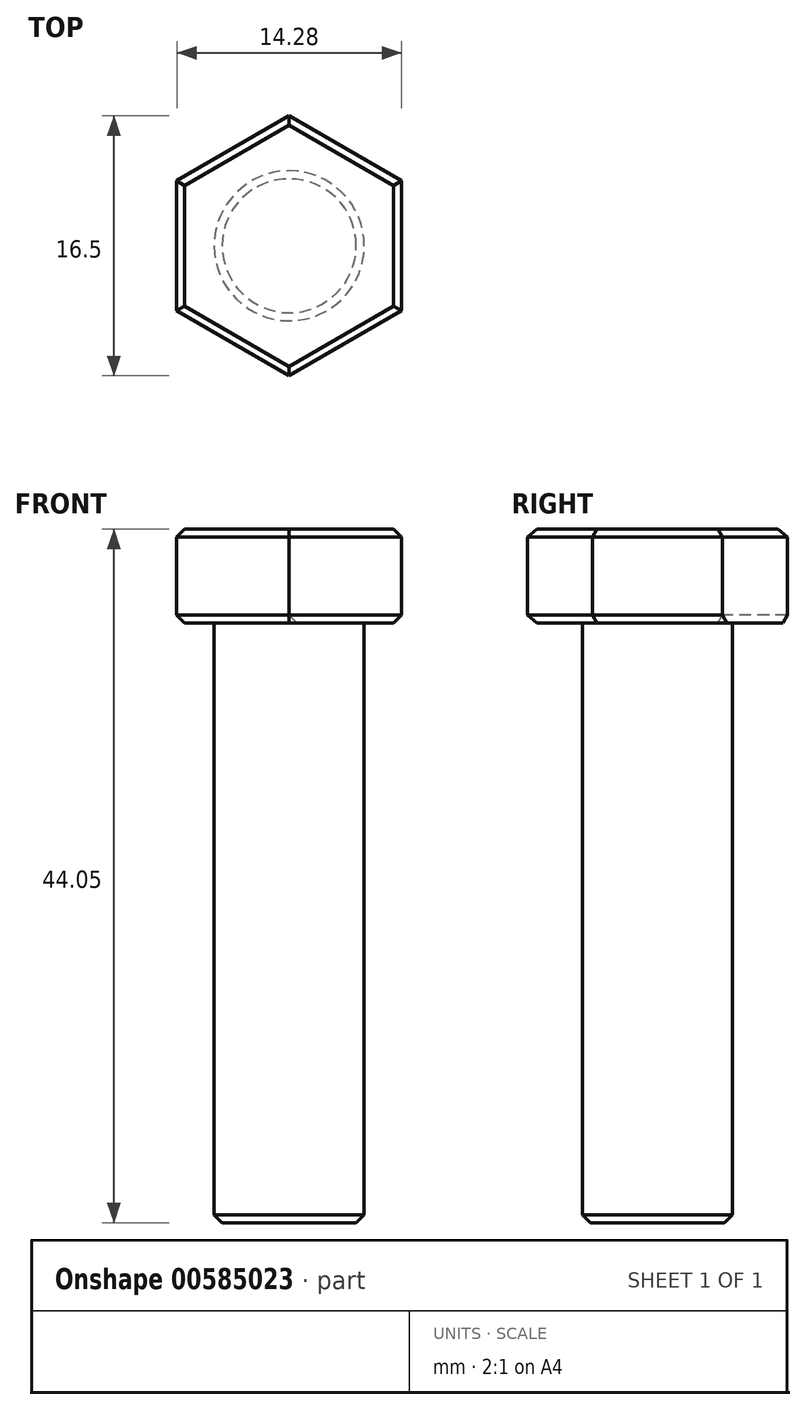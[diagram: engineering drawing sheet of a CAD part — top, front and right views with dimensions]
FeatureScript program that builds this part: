
annotation { "Feature Type Name" : "Feature", "Feature Type Description" : "" }
export const myFeature = defineFeature(function(context is Context, id is Id, definition is map)
    precondition{}
    {
        {
            var Q0;
            Q0=qCreatedBy(makeId("Top.planeOp"),FACE);
            var sketch = newSketch(context, id + "F0", { "sketchPlane" : qUnion([Q0])});
            skCircle(sketch, "E0.cCircle", {"center": v(0, 0) * mm, "radius": 7.14 * mm, "construction": true});
            skLineSegment(sketch, "E0.0", {"start": v(7.14, 4.12) * mm, "end": v(7.14, -4.12) * mm});
            skLineSegment(sketch, "E0.1", {"start": v(7.14, -4.12) * mm, "end": v(0, -8.25) * mm});
            skLineSegment(sketch, "E0.2", {"start": v(0, -8.25) * mm, "end": v(-7.14, -4.12) * mm});
            skLineSegment(sketch, "E0.3", {"start": v(-7.14, -4.12) * mm, "end": v(-7.14, 4.12) * mm});
            skLineSegment(sketch, "E0.4", {"start": v(-7.14, 4.12) * mm, "end": v(0, 8.25) * mm});
            skLineSegment(sketch, "E0.5", {"start": v(0, 8.25) * mm, "end": v(7.14, 4.12) * mm});
            skPoint(sketch, "E0.0.midPoint", {"position": v(7.14, 0) * mm});
            skCircle(sketch, "E1", {"center": v(0, 0) * mm, "radius": 4.76 * mm});
            skSolve(sketch);
        }
        {
            var Q0;
            Q0 = qSketchRegion(id + "F0", true);
            var Q1;
            Q1=makeQuery(id+"F0.imprint","IMPRINT",FACE,{"disambiguationData":[TD([[makeQuery(id+"F0.imprint","IMPRINT",EDGE,{"derivedFrom":sQuery(id+"F0.wireOp",EDGE,"E1")}),1.0]])]});
            extrude(context, id + "F1", {"entities" : qUnion([Q0, Q1]), "depth" : 5.95 * mm, "offsetDistance" : 25.4 * mm});
        }
        {
            var Q0;
            Q0=makeQuery(id+"F0.imprint","IMPRINT",FACE,{"disambiguationData":[TD([[makeQuery(id+"F0.imprint","IMPRINT",EDGE,{"derivedFrom":sQuery(id+"F0.wireOp",EDGE,"E1")}),1.0]])]});
            extrude(context, id + "F2", {"entities" : qUnion([Q0]), "operationType" : NewBodyOperationType.ADD, "oppositeDirection" : true, "depth" : 38.1 * mm, "offsetDistance" : 25.4 * mm});
        }
        {
            var Q0;
            Q0=makeQuery(id+"F2.opExtrude","CAP_EDGE",EDGE,{"disambiguationData":[OSD([sQuery(id+"F0.wireOp",EDGE,"E1")])],"isStart":false});
            chamfer(context, id + "F3", {"entities" : qUnion([Q0]), "width" : 0.5 * mm, "tangentPropagation" : true});
        }
        {
            var Q0;
            Q0=makeQuery(id+"F1.opExtrude","CAP_FACE",FACE,{"disambiguationData":[OSD([sQuery(id+"F0.wireOp",EDGE,"E0.0"),sQuery(id+"F0.wireOp",EDGE,"E0.1"),sQuery(id+"F0.wireOp",EDGE,"E0.2"),sQuery(id+"F0.wireOp",EDGE,"E0.3"),sQuery(id+"F0.wireOp",EDGE,"E0.4"),sQuery(id+"F0.wireOp",EDGE,"E0.5")])],"isStart":false});
            var Q1;
            Q1=makeQuery(id+"F1.opExtrude","CAP_EDGE",EDGE,{"disambiguationData":[OSD([sQuery(id+"F0.wireOp",EDGE,"E0.2")])],"isStart":true});
            var Q2;
            Q2=makeQuery(id+"F1.opExtrude","CAP_EDGE",EDGE,{"disambiguationData":[OSD([sQuery(id+"F0.wireOp",EDGE,"E0.1")])],"isStart":true});
            var Q3;
            Q3=makeQuery(id+"F1.opExtrude","CAP_EDGE",EDGE,{"disambiguationData":[OSD([sQuery(id+"F0.wireOp",EDGE,"E0.0")])],"isStart":true});
            var Q4;
            Q4=makeQuery(id+"F1.opExtrude","CAP_EDGE",EDGE,{"disambiguationData":[OSD([sQuery(id+"F0.wireOp",EDGE,"E0.3")])],"isStart":true});
            var Q5;
            Q5=makeQuery(id+"F1.opExtrude","CAP_EDGE",EDGE,{"disambiguationData":[OSD([sQuery(id+"F0.wireOp",EDGE,"E0.4")])],"isStart":true});
            chamfer(context, id + "F4", {"entities" : qUnion([Q0, Q1, Q2, Q3, Q4, Q5]), "width" : 0.5 * mm, "tangentPropagation" : true});
        }
    });
